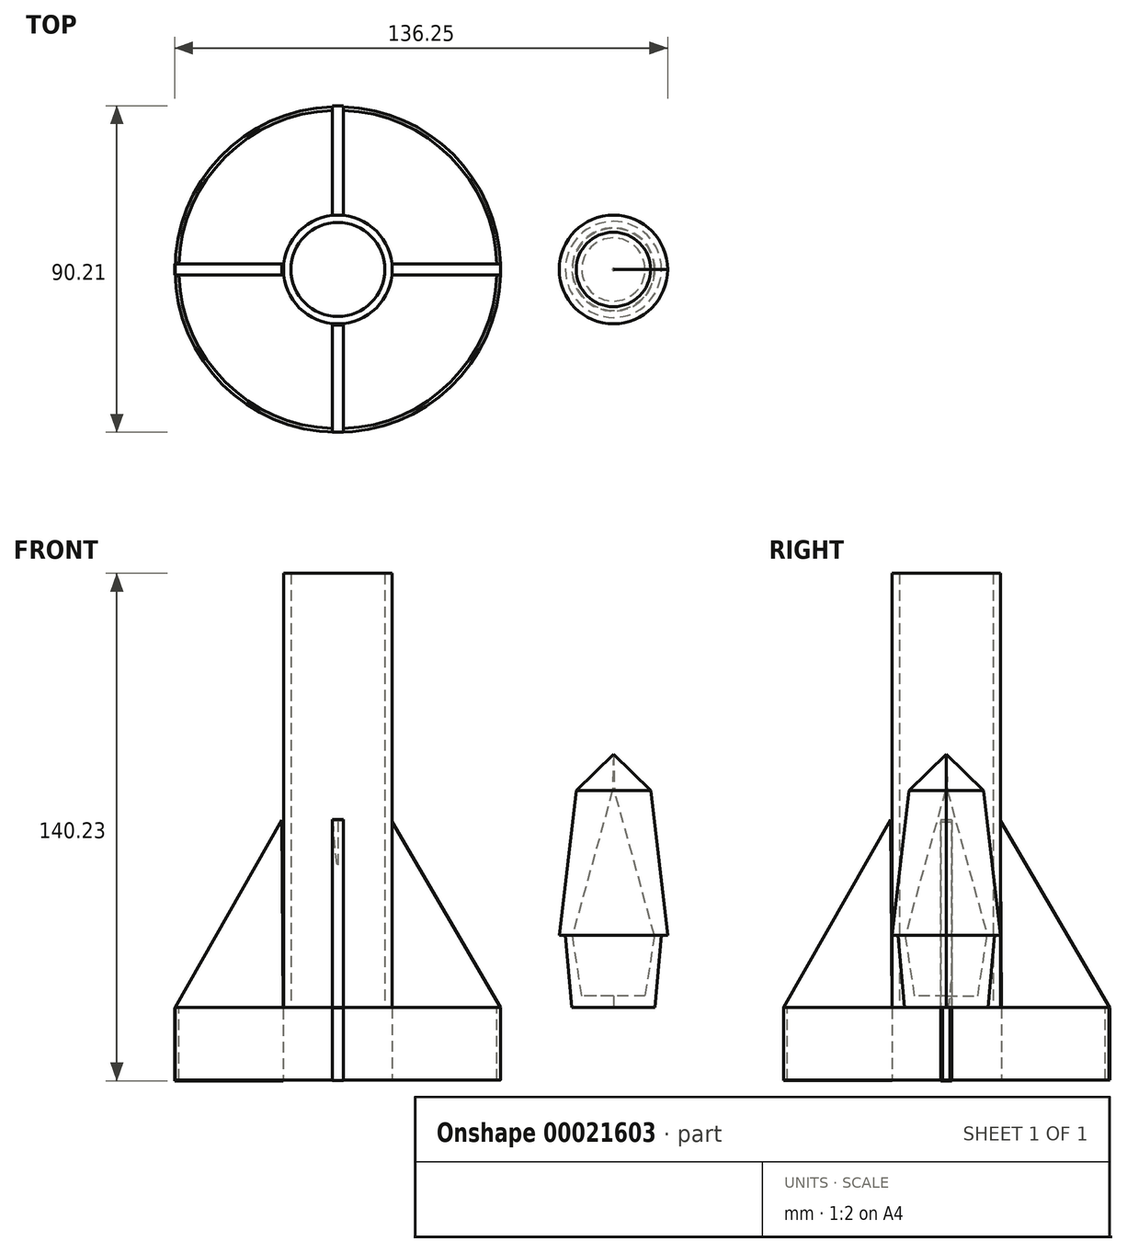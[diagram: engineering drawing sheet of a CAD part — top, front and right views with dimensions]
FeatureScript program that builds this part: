
annotation { "Feature Type Name" : "Feature", "Feature Type Description" : "" }
export const myFeature = defineFeature(function(context is Context, id is Id, definition is map)
    precondition{}
    {
        {
            var Q0;
            Q0=qCreatedBy(makeId("Top.planeOp"),FACE);
            var sketch = newSketch(context, id + "F0", { "sketchPlane" : qUnion([Q0])});
            skCircle(sketch, "E0", {"center": v(0, 0) * mm, "radius": 15 * mm});
            skSolve(sketch);
        }
        {
            var Q0;
            Q0 = qSketchRegion(id + "F0", true);
            extrude(context, id + "F1", {"entities" : qUnion([Q0]), "depth" : 120 * mm});
        }
        {
            var Q0;
            Q0=qCreatedBy(makeId("Top.planeOp"),FACE);
            var sketch = newSketch(context, id + "F2", { "sketchPlane" : qUnion([Q0])});
            skCircle(sketch, "E1", {"center": v(0, 0) * mm, "radius": 13 * mm});
            skSolve(sketch);
        }
        {
            var Q0;
            Q0 = qSketchRegion(id + "F2", true);
            extrude(context, id + "F3", {"entities" : qUnion([Q0]), "operationType" : NewBodyOperationType.REMOVE, "depth" : 120 * mm});
        }
        {
            var Q0;
            Q0=qCreatedBy(makeId("Front.planeOp"),FACE);
            var sketch = newSketch(context, id + "F4", { "sketchPlane" : qUnion([Q0])});
            skLineSegment(sketch, "E2.bottom", {"start": v(14.99, 0) * mm, "end": v(44.99, 0) * mm});
            skLineSegment(sketch, "E2.top", {"start": v(14.99, -20) * mm, "end": v(44.99, -20) * mm});
            skLineSegment(sketch, "E2.left", {"start": v(14.99, 0) * mm, "end": v(14.99, -20) * mm});
            skLineSegment(sketch, "E2.right", {"start": v(44.99, 0) * mm, "end": v(44.99, -20) * mm});
            skLineSegment(sketch, "E3.bottom", {"start": v(-45.1, -0.23) * mm, "end": v(-15.1, -0.23) * mm});
            skLineSegment(sketch, "E3.top", {"start": v(-45.1, -20.23) * mm, "end": v(-15.1, -20.23) * mm});
            skLineSegment(sketch, "E3.left", {"start": v(-45.1, -0.23) * mm, "end": v(-45.1, -20.23) * mm});
            skLineSegment(sketch, "E3.right", {"start": v(-15.1, -0.23) * mm, "end": v(-15.1, -20.23) * mm});
            skLineSegment(sketch, "E4", {"start": v(44.99, 0) * mm, "end": v(14.7, 51.8) * mm});
            skLineSegment(sketch, "E5", {"start": v(-15.43, 51.91) * mm, "end": v(-45.1, -0.23) * mm});
            skLineSegment(sketch, "E6", {"start": v(-15.43, 51.91) * mm, "end": v(-15.1, -0.23) * mm});
            skLineSegment(sketch, "E7", {"start": v(14.7, 51.8) * mm, "end": v(14.99, 0) * mm});
            skSolve(sketch);
        }
        {
            var Q0;
            Q0 = qSketchRegion(id + "F4", true);
            extrude(context, id + "F5", {"entities" : qUnion([Q0]), "operationType" : NewBodyOperationType.ADD, "oppositeDirection" : true, "depth" : 1.5 * mm});
        }
        {
            var Q0;
            Q0=makeQuery(id+"F5.opExtrude","CAP_FACE",FACE,{"disambiguationData":[OSD([sQuery(id+"F4.wireOp",EDGE,"E3.bottom"),sQuery(id+"F4.wireOp",EDGE,"E3.top"),sQuery(id+"F4.wireOp",EDGE,"E3.left"),sQuery(id+"F4.wireOp",EDGE,"E3.right")])],"isStart":true});
            var Q1;
            Q1=makeQuery(id+"F5.opExtrude","CAP_FACE",FACE,{"disambiguationData":[OSD([sQuery(id+"F4.wireOp",EDGE,"E2.bottom"),sQuery(id+"F4.wireOp",EDGE,"E2.top"),sQuery(id+"F4.wireOp",EDGE,"E2.left"),sQuery(id+"F4.wireOp",EDGE,"E2.right")])],"isStart":true});
            extrude(context, id + "F6", {"entities" : qUnion([Q0, Q1]), "operationType" : NewBodyOperationType.ADD, "depth" : 1.5 * mm});
        }
        {
            var Q0;
            Q0=qCreatedBy(makeId("Right.planeOp"),FACE);
            var sketch = newSketch(context, id + "F7", { "sketchPlane" : qUnion([Q0])});
            skLineSegment(sketch, "E8.left", {"start": v(15.21, -0.07) * mm, "end": v(15.21, -20.07) * mm});
            skLineSegment(sketch, "E8.top", {"start": v(15.21, -20.07) * mm, "end": v(45.21, -20.07) * mm});
            skLineSegment(sketch, "E9", {"start": v(45.21, -0.07) * mm, "end": v(14.93, 51.73) * mm});
            skLineSegment(sketch, "E10", {"start": v(14.93, 51.73) * mm, "end": v(15.21, -0.07) * mm});
            skLineSegment(sketch, "E8.right", {"start": v(45.21, -0.07) * mm, "end": v(45.21, -20.07) * mm});
            skLineSegment(sketch, "E8.bottom", {"start": v(15.21, -0.07) * mm, "end": v(45.21, -0.07) * mm});
            skLineSegment(sketch, "E11", {"start": v(-15.33, 52) * mm, "end": v(-45, -0.14) * mm});
            skLineSegment(sketch, "E12", {"start": v(-15.33, 52) * mm, "end": v(-15, -0.14) * mm});
            skLineSegment(sketch, "E13.left", {"start": v(-45, -0.14) * mm, "end": v(-45, -20.14) * mm});
            skLineSegment(sketch, "E13.bottom", {"start": v(-45, -0.14) * mm, "end": v(-15, -0.14) * mm});
            skLineSegment(sketch, "E13.top", {"start": v(-45, -20.14) * mm, "end": v(-15, -20.14) * mm});
            skLineSegment(sketch, "E13.right", {"start": v(-15, -0.14) * mm, "end": v(-15, -20.14) * mm});
            skSolve(sketch);
        }
        {
            var Q0;
            Q0=makeQuery(id+"F7.imprint","IMPRINT",FACE,{"disambiguationData":[TD([[makeQuery(id+"F7.imprint","IMPRINT",EDGE,{"derivedFrom":sQuery(id+"F7.wireOp",EDGE,"E8.left")}),1.0]])]});
            var Q1;
            Q1=makeQuery(id+"F7.imprint","IMPRINT",FACE,{"disambiguationData":[TD([[makeQuery(id+"F7.imprint","IMPRINT",EDGE,{"derivedFrom":sQuery(id+"F7.wireOp",EDGE,"E13.left")}),1.0]])]});
            var Q2;
            Q2=makeQuery(id+"F7.imprint","IMPRINT",FACE,{"disambiguationData":[TD([[makeQuery(id+"F7.imprint","IMPRINT",EDGE,{"derivedFrom":sQuery(id+"F7.wireOp",EDGE,"E11")}),1.0]])]});
            var Q3;
            Q3=makeQuery(id+"F7.imprint","IMPRINT",FACE,{"disambiguationData":[TD([[makeQuery(id+"F7.imprint","IMPRINT",EDGE,{"derivedFrom":sQuery(id+"F7.wireOp",EDGE,"E9")}),1.0]])]});
            extrude(context, id + "F8", {"entities" : qUnion([Q0, Q1, Q2, Q3]), "operationType" : NewBodyOperationType.ADD, "oppositeDirection" : true, "depth" : 1.5 * mm});
        }
        {
            var Q0;
            Q0=makeQuery(id+"F8.opExtrude","CAP_FACE",FACE,{"disambiguationData":[OSD([sQuery(id+"F7.wireOp",EDGE,"E11"),sQuery(id+"F7.wireOp",EDGE,"E12"),sQuery(id+"F7.wireOp",EDGE,"E13.left"),sQuery(id+"F7.wireOp",EDGE,"E13.top"),sQuery(id+"F7.wireOp",EDGE,"E13.right")])],"isStart":true});
            var Q1;
            Q1=makeQuery(id+"F8.opExtrude","CAP_FACE",FACE,{"disambiguationData":[OSD([sQuery(id+"F7.wireOp",EDGE,"E8.left"),sQuery(id+"F7.wireOp",EDGE,"E8.top"),sQuery(id+"F7.wireOp",EDGE,"E9"),sQuery(id+"F7.wireOp",EDGE,"E10"),sQuery(id+"F7.wireOp",EDGE,"E8.right")])],"isStart":true});
            var Q2;
            Q2 = qSketchRegion(id + "F10", true);
            extrude(context, id + "F9", {"entities" : qUnion([Q0, Q1, Q2]), "operationType" : NewBodyOperationType.ADD, "depth" : 1.5 * mm});
        }
        {
            var Q0;
            Q0=qCreatedBy(makeId("Top.planeOp"),FACE);
            var sketch = newSketch(context, id + "F10", { "sketchPlane" : qUnion([Q0])});
            skCircle(sketch, "E14", {"center": v(0, 0) * mm, "radius": 45 * mm});
            skCircle(sketch, "E15", {"center": v(0, 0) * mm, "radius": 44 * mm});
            skSolve(sketch);
        }
        {
            var Q0;
            Q0=makeQuery(id+"F10.imprint","IMPRINT",FACE,{"disambiguationData":[TD([[makeQuery(id+"F10.imprint","IMPRINT",EDGE,{"derivedFrom":sQuery(id+"F10.wireOp",EDGE,"E14")}),1.0]])]});
            extrude(context, id + "F11", {"entities" : qUnion([Q0]), "operationType" : NewBodyOperationType.ADD, "oppositeDirection" : true, "depth" : 20 * mm});
        }
        {
            var Q0;
            Q0=qCreatedBy(makeId("Front.planeOp"),FACE);
            var sketch = newSketch(context, id + "F12", { "sketchPlane" : qUnion([Q0])});
            skLineSegment(sketch, "E16.left", {"start": v(76.15, 70) * mm, "end": v(75.87, 60) * mm});
            skLineSegment(sketch, "E17", {"start": v(76.15, 70) * mm, "end": v(65.87, 60) * mm});
            skLineSegment(sketch, "E18", {"start": v(65.87, 60) * mm, "end": v(61.15, 20) * mm});
            skLineSegment(sketch, "E19", {"start": v(64.83, 20) * mm, "end": v(75.87, 60) * mm});
            skLineSegment(sketch, "E20", {"start": v(76.15, 0) * mm, "end": v(64.65, 0) * mm});
            skLineSegment(sketch, "E21.bottom", {"start": v(61.15, 20) * mm, "end": v(62.87, 20) * mm});
            skLineSegment(sketch, "E22", {"start": v(62.87, 20) * mm, "end": v(64.65, 0) * mm});
            skLineSegment(sketch, "E23.trimOffspring", {"start": v(76.15, 3.22) * mm, "end": v(76.15, 0) * mm});
            skLineSegment(sketch, "E24.trimOffspring", {"start": v(62.87, 20) * mm, "end": v(61.15, 20) * mm});
            skLineSegment(sketch, "E25", {"start": v(64.83, 20) * mm, "end": v(67.43, 3.26) * mm});
            skLineSegment(sketch, "E26", {"start": v(67.43, 3.26) * mm, "end": v(76.15, 3.22) * mm});
            skSolve(sketch);
        }
        {
            var Q0;
            Q0=makeQuery(id+"F12.imprint","IMPRINT",FACE,{"disambiguationData":[TD([[makeQuery(id+"F12.imprint","IMPRINT",EDGE,{"derivedFrom":sQuery(id+"F12.wireOp",EDGE,"E17")}),1.0]])]});
            var Q1;
            Q1=sQuery(id+"F12.wireOp",EDGE,"E18");
            var Q2;
            Q2=sQuery(id+"F12.wireOp",EDGE,"E17");
            var Q3;
            Q3=sQuery(id+"F12.wireOp",EDGE,"E22");
            var Q4;
            Q4=sQuery(id+"F12.wireOp",EDGE,"E21.bottom");
            var Q5;
            Q5=sQuery(id+"F12.wireOp",EDGE,"E19");
            var Q6;
            Q6=sQuery(id+"F12.wireOp",EDGE,"E25");
            var Q7;
            Q7=sQuery(id+"F12.wireOp",EDGE,"E26");
            var Q8;
            Q8=sQuery(id+"F12.wireOp",EDGE,"E20");
            var Q9;
            Q9=sQuery(id+"F12.wireOp",EDGE,"E23.trimOffspring");
            revolve(context, id + "F13", {"entities" : qUnion([Q0]), "surfaceEntities" : qUnion([Q1, Q2, Q3, Q4, Q5, Q6, Q7, Q8]), "axis" : qUnion([Q9]), "revolveType" : RevolveType.SYMMETRIC, "oppositeDirection" : true, "angle" : 360 * degree});
        }
    });
